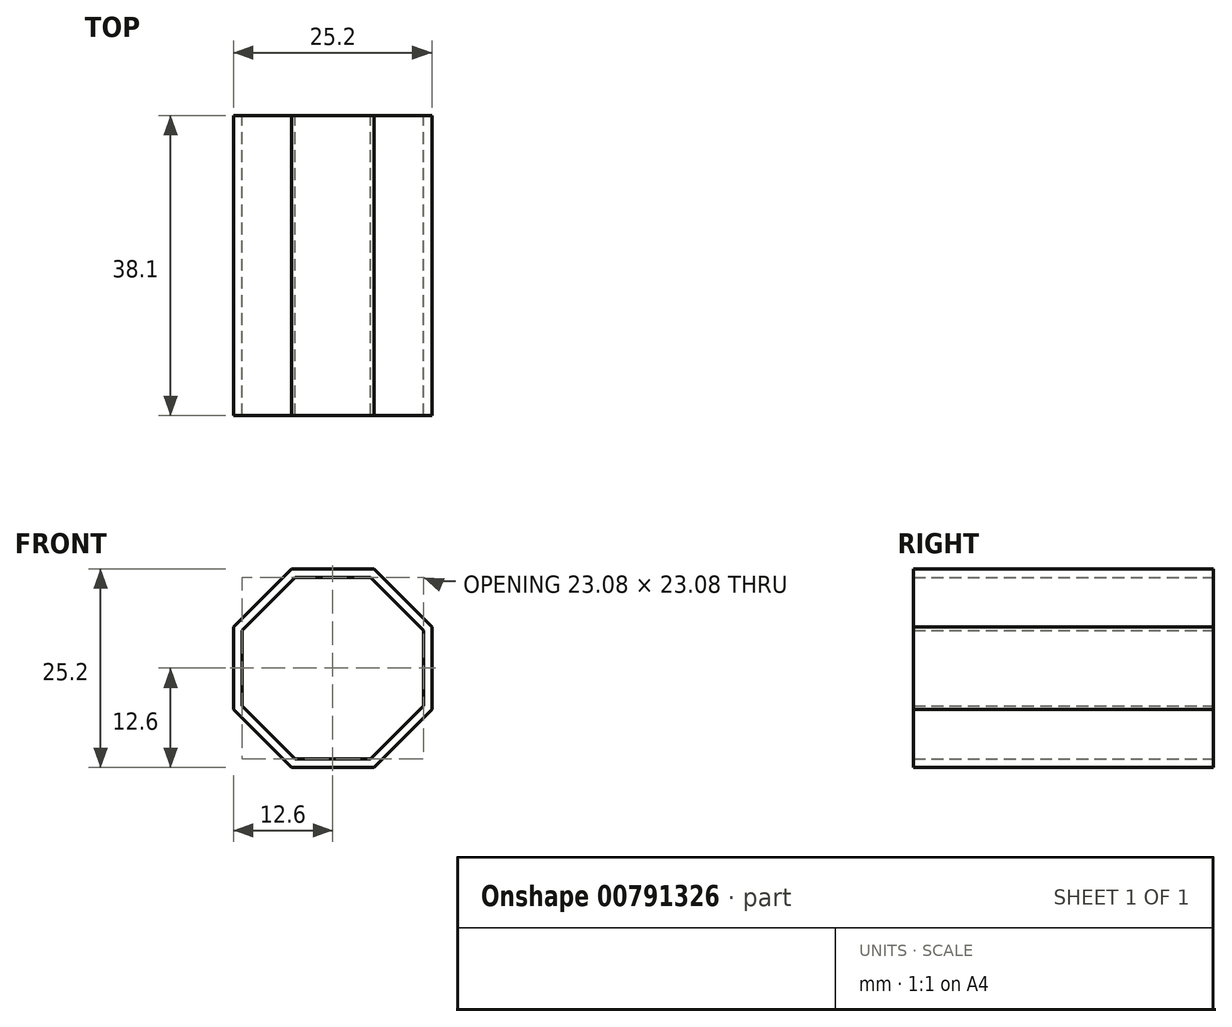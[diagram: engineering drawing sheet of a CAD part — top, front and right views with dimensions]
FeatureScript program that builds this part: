
annotation { "Feature Type Name" : "Feature", "Feature Type Description" : "" }
export const myFeature = defineFeature(function(context is Context, id is Id, definition is map)
    precondition{}
    {
        {
            var Q0;
            Q0=qCreatedBy(makeId("Front.planeOp"),FACE);
            var sketch = newSketch(context, id + "F0", { "sketchPlane" : qUnion([Q0])});
            skPoint(sketch, "E0", {"position": v(0, 12.6) * mm});
            skPoint(sketch, "E1", {"position": v(0, -12.6) * mm});
            skPoint(sketch, "E2", {"position": v(-12.6, 0) * mm});
            skPoint(sketch, "E3", {"position": v(12.6, 0) * mm});
            skLineSegment(sketch, "E4", {"start": v(0, 0) * mm, "end": v(-8.9, 8.9) * mm});
            skLineSegment(sketch, "E5", {"start": v(-8.9, -8.9) * mm, "end": v(0, 0) * mm});
            skLineSegment(sketch, "E6", {"start": v(8.9, 8.9) * mm, "end": v(0, 0) * mm});
            skLineSegment(sketch, "E7", {"start": v(8.9, -8.9) * mm, "end": v(0, 0) * mm});
            skLineSegment(sketch, "E8", {"start": v(0, 12.6) * mm, "end": v(0, 0) * mm, "construction": true});
            skPoint(sketch, "E9", {"position": v(-8.9, 8.9) * mm});
            skPoint(sketch, "E10", {"position": v(-8.9, -8.9) * mm});
            skPoint(sketch, "E11", {"position": v(8.9, -8.9) * mm});
            skPoint(sketch, "E12", {"position": v(8.9, 8.9) * mm});
            skLineSegment(sketch, "E13", {"start": v(12.6, 5.22) * mm, "end": v(12.6, -5.22) * mm});
            skLineSegment(sketch, "E14", {"start": v(-5.22, -12.6) * mm, "end": v(5.22, -12.6) * mm});
            skLineSegment(sketch, "E15", {"start": v(-12.6, 5.22) * mm, "end": v(-5.22, 12.6) * mm});
            skLineSegment(sketch, "E16", {"start": v(5.22, 12.6) * mm, "end": v(12.6, 5.22) * mm});
            skLineSegment(sketch, "E17", {"start": v(12.6, -5.22) * mm, "end": v(5.22, -12.6) * mm});
            skLineSegment(sketch, "E18", {"start": v(-12.6, -5.22) * mm, "end": v(-5.22, -12.6) * mm});
            skLineSegment(sketch, "E19.trimOffspring", {"start": v(-5.22, 12.6) * mm, "end": v(5.22, 12.6) * mm});
            skLineSegment(sketch, "E20.trimOffspring", {"start": v(-12.6, 5.22) * mm, "end": v(-12.6, -5.22) * mm});
            skPoint(sketch, "E21.start.orphan", {"position": v(-13.66, 12.6) * mm});
            skPoint(sketch, "E22.start.orphan", {"position": v(-12.6, 14.7) * mm});
            skPoint(sketch, "E23.orphan", {"position": v(-13.6, -12.6) * mm});
            skPoint(sketch, "E24.orphan", {"position": v(12.6, 15.56) * mm});
            skPoint(sketch, "E25.orphan", {"position": v(17.81, 0) * mm});
            skPoint(sketch, "E26", {"position": v(0, 0) * mm});
            skPoint(sketch, "E27", {"position": v(-12.6, 5.22) * mm});
            skPoint(sketch, "E28", {"position": v(-5.22, 12.6) * mm});
            skPoint(sketch, "E29", {"position": v(5.22, 12.6) * mm});
            skPoint(sketch, "E30", {"position": v(12.6, 5.22) * mm});
            skPoint(sketch, "E31", {"position": v(12.6, -5.22) * mm});
            skPoint(sketch, "E32", {"position": v(5.22, -12.6) * mm});
            skPoint(sketch, "E33", {"position": v(-5.22, -12.6) * mm});
            skPoint(sketch, "E34", {"position": v(-12.6, -5.22) * mm});
            skLineSegment(sketch, "E35", {"start": v(0, 0) * mm, "end": v(5.22, 12.6) * mm, "construction": true});
            skLineSegment(sketch, "E36", {"start": v(0, 0) * mm, "end": v(12.6, 5.22) * mm, "construction": true});
            skLineSegment(sketch, "E37", {"start": v(0, 0) * mm, "end": v(12.6, -5.22) * mm, "construction": true});
            skLineSegment(sketch, "E38", {"start": v(0, 0) * mm, "end": v(5.22, -12.6) * mm, "construction": true});
            skLineSegment(sketch, "E39", {"start": v(0, 0) * mm, "end": v(0, -12.6) * mm, "construction": true});
            skLineSegment(sketch, "E40.MirrorCS", {"start": v(0, 0) * mm, "end": v(-5.22, 12.6) * mm, "construction": true});
            skLineSegment(sketch, "E41.MirrorCS", {"start": v(0, 0) * mm, "end": v(-12.6, 5.22) * mm, "construction": true});
            skLineSegment(sketch, "E42.MirrorCS", {"start": v(0, 0) * mm, "end": v(-12.6, -5.22) * mm, "construction": true});
            skLineSegment(sketch, "E43.MirrorCS", {"start": v(0, 0) * mm, "end": v(-5.22, -12.6) * mm, "construction": true});
            skPoint(sketch, "E44", {"position": v(-11.54, 4.78) * mm});
            skLineSegment(sketch, "E45", {"start": v(-11.54, 4.78) * mm, "end": v(-11.54, -4.78) * mm});
            skLineSegment(sketch, "E46", {"start": v(-11.54, -4.78) * mm, "end": v(-4.78, -11.54) * mm});
            skLineSegment(sketch, "E47", {"start": v(-4.78, -11.54) * mm, "end": v(4.78, -11.54) * mm});
            skLineSegment(sketch, "E48", {"start": v(4.78, -11.54) * mm, "end": v(11.54, -4.78) * mm});
            skLineSegment(sketch, "E49", {"start": v(11.54, -4.78) * mm, "end": v(11.54, 4.78) * mm});
            skLineSegment(sketch, "E50", {"start": v(11.54, 4.78) * mm, "end": v(4.78, 11.54) * mm});
            skLineSegment(sketch, "E51", {"start": v(4.78, 11.54) * mm, "end": v(-4.78, 11.54) * mm});
            skLineSegment(sketch, "E52", {"start": v(-4.78, 11.54) * mm, "end": v(-11.54, 4.78) * mm});
            skSolve(sketch);
        }
        {
            var Q0;
            {var subQ3=sQuery(id+"F0.wireOp",EDGE,"E19.trimOffspring");Q0=makeQuery(id+"F0.imprint","IMPRINT",FACE,{"disambiguationData":[TD([[makeQuery(id+"F0.imprint","IMPRINT",EDGE,{"derivedFrom":subQ3}),-1.0]])]});}
            var Q1;
            {var subQ3=sQuery(id+"F0.wireOp",EDGE,"E20.trimOffspring");Q1=makeQuery(id+"F0.imprint","IMPRINT",FACE,{"disambiguationData":[TD([[makeQuery(id+"F0.imprint","IMPRINT",EDGE,{"derivedFrom":subQ3}),1.0]])]});}
            var Q2;
            {var subQ3=sQuery(id+"F0.wireOp",EDGE,"E13");Q2=makeQuery(id+"F0.imprint","IMPRINT",FACE,{"disambiguationData":[TD([[makeQuery(id+"F0.imprint","IMPRINT",EDGE,{"derivedFrom":subQ3}),-1.0]])]});}
            var Q3;
            {var subQ3=sQuery(id+"F0.wireOp",EDGE,"E14");Q3=makeQuery(id+"F0.imprint","IMPRINT",FACE,{"disambiguationData":[TD([[makeQuery(id+"F0.imprint","IMPRINT",EDGE,{"derivedFrom":subQ3}),1.0]])]});}
            extrude(context, id + "F1", {"entities" : qUnion([Q0, Q1, Q2, Q3]), "endBound" : BoundingType.SYMMETRIC, "depth" : 38.1 * mm, "offsetDistance" : 25.4 * mm});
        }
    });
